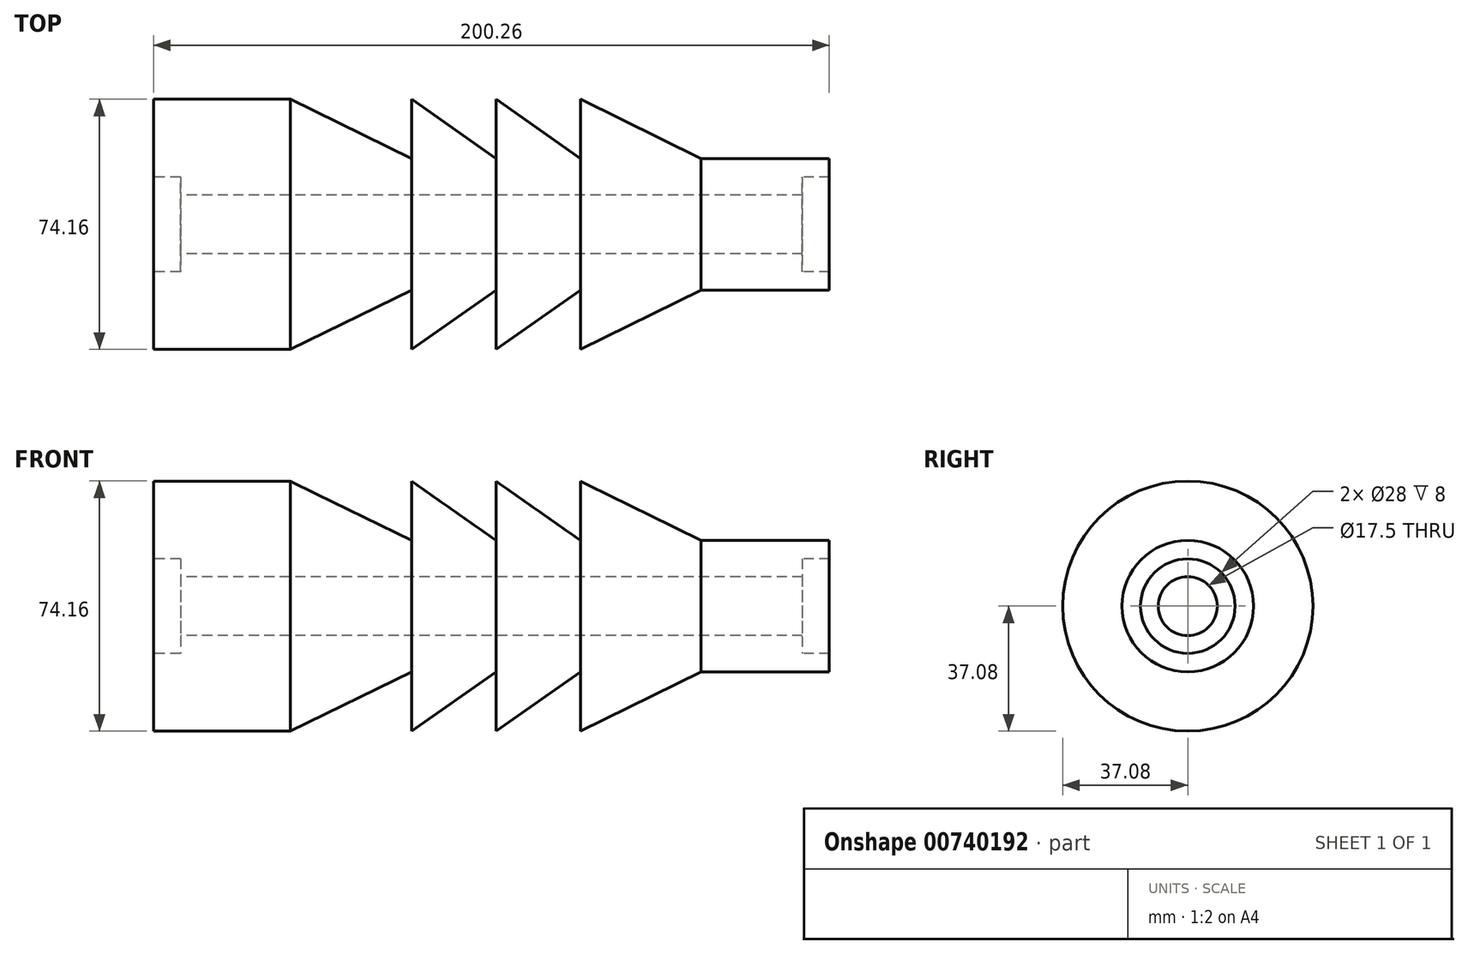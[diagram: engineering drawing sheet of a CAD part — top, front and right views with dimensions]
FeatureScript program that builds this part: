
annotation { "Feature Type Name" : "Feature", "Feature Type Description" : "" }
export const myFeature = defineFeature(function(context is Context, id is Id, definition is map)
    precondition{}
    {
        {
            var Q0;
            Q0=qCreatedBy(makeId("Front.planeOp"),FACE);
            var sketch = newSketch(context, id + "F0", { "sketchPlane" : qUnion([Q0])});
            skLineSegment(sketch, "E0", {"start": v(-100.12, 0) * mm, "end": v(100.13, 0) * mm, "construction": true});
            skPoint(sketch, "E1", {"position": v(0, 0) * mm});
            skLineSegment(sketch, "E2", {"start": v(-92.12, 14) * mm, "end": v(-100.12, 14) * mm});
            skLineSegment(sketch, "E3", {"start": v(-100.13, 14) * mm, "end": v(-100.13, 37.08) * mm});
            skLineSegment(sketch, "E4", {"start": v(-100.13, 37.08) * mm, "end": v(-59.63, 37.08) * mm});
            skLineSegment(sketch, "E5", {"start": v(-59.63, 37.08) * mm, "end": v(-23.63, 19.5) * mm});
            skLineSegment(sketch, "E6", {"start": v(-23.63, 19.5) * mm, "end": v(-23.63, 37.08) * mm});
            skLineSegment(sketch, "E7", {"start": v(-23.63, 37.08) * mm, "end": v(1.37, 19.5) * mm});
            skLineSegment(sketch, "E8", {"start": v(1.37, 19.5) * mm, "end": v(1.37, 37.08) * mm});
            skLineSegment(sketch, "E9", {"start": v(1.37, 37.08) * mm, "end": v(26.37, 19.5) * mm});
            skLineSegment(sketch, "E10", {"start": v(26.37, 19.5) * mm, "end": v(26.37, 37.08) * mm});
            skLineSegment(sketch, "E11", {"start": v(26.37, 37.08) * mm, "end": v(62.12, 19.5) * mm});
            skLineSegment(sketch, "E12", {"start": v(62.12, 19.5) * mm, "end": v(100.13, 19.5) * mm});
            skLineSegment(sketch, "E13", {"start": v(100.13, 19.5) * mm, "end": v(100.13, 14) * mm});
            skLineSegment(sketch, "E14", {"start": v(100.12, 14) * mm, "end": v(92.13, 14) * mm});
            skLineSegment(sketch, "E15", {"start": v(-92.12, 14) * mm, "end": v(-92.12, 8.75) * mm});
            skLineSegment(sketch, "E16", {"start": v(92.13, 14) * mm, "end": v(92.13, 8.75) * mm});
            skLineSegment(sketch, "E17", {"start": v(-92.12, 8.75) * mm, "end": v(92.13, 8.75) * mm});
            skSolve(sketch);
        }
        {
            var Q0;
            Q0=makeQuery(id+"F0.imprint","IMPRINT",FACE,{"disambiguationData":[TD([[makeQuery(id+"F0.imprint","IMPRINT",EDGE,{"derivedFrom":sQuery(id+"F0.wireOp",EDGE,"E2")}),-1.0]])]});
            var Q1;
            Q1=sQuery(id+"F0.wireOp",EDGE,"E0");
            revolve(context, id + "F1", {"surfaceOperationType" : NewSurfaceOperationType.NEW, "entities" : qUnion([Q0]), "axis" : qUnion([Q1]), "revolveType" : RevolveType.FULL});
        }
    });
